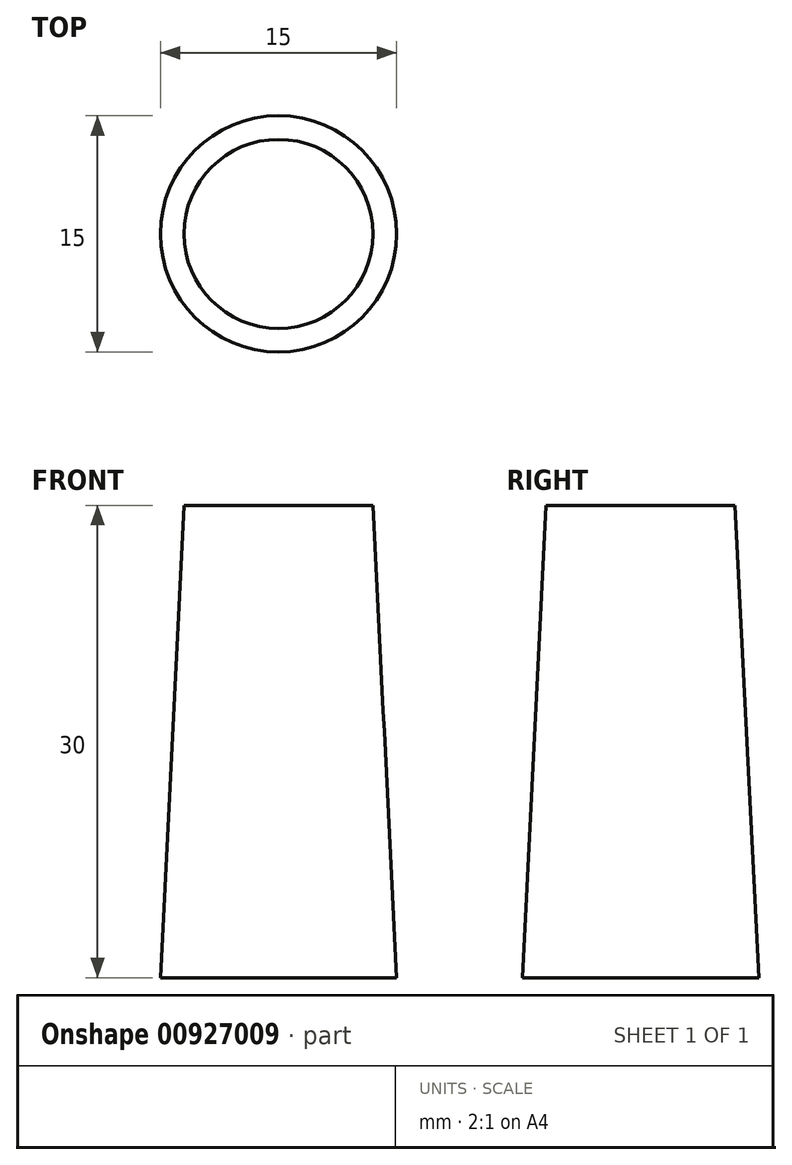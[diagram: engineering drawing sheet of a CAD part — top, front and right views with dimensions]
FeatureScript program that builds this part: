
annotation { "Feature Type Name" : "Feature", "Feature Type Description" : "" }
export const myFeature = defineFeature(function(context is Context, id is Id, definition is map)
    precondition{}
    {
        {
            assignVariable(context, id + "F0", {"name" : "height", "anyValue" : 30});
        }
        {
            var Q0;
            Q0=qCreatedBy(makeId("Top.planeOp"),FACE);
            cPlane(context, id + "F1", {"entities" : qUnion([Q0]), "cplaneType" : CPlaneType.OFFSET, "offset" : (getVariable(context, 'height')) * mm, "oppositeDirection" : true, "width" : 150 * mm, "height" : 150 * mm});
        }
        {
            var Q0;
            Q0=qCreatedBy(makeId("Top.planeOp"),FACE);
            var sketch = newSketch(context, id + "F2", { "sketchPlane" : qUnion([Q0])});
            skCircle(sketch, "E0", {"center": v(0, 0) * mm, "radius": 6 * mm});
            skSolve(sketch);
        }
        {
            var Q0;
            Q0=qCreatedBy(id+"F1.planeOp",FACE);
            var sketch = newSketch(context, id + "F3", { "sketchPlane" : qUnion([Q0])});
            skPoint(sketch, "E1.0", {"position": v(0, 0) * mm});
            skCircle(sketch, "E2", {"center": v(0, 0) * mm, "radius": 7.5 * mm});
            skSolve(sketch);
        }
        {
            var Q0;
            Q0=makeQuery(id+"F2.imprint","IMPRINT",FACE,{"disambiguationData":[TD([[makeQuery(id+"F2.imprint","IMPRINT",EDGE,{"derivedFrom":sQuery(id+"F2.wireOp",EDGE,"E0")}),1.0]])]});
            var Q1;
            Q1=makeQuery(id+"F3.imprint","IMPRINT",FACE,{"disambiguationData":[TD([[makeQuery(id+"F3.imprint","IMPRINT",EDGE,{"derivedFrom":sQuery(id+"F3.wireOp",EDGE,"E2")}),1.0]])]});
            loft(context, id + "F4", {"sheetProfilesArray" : [{ "sheetProfileEntities" : qUnion([Q0]) }, { "sheetProfileEntities" : qUnion([Q1]) }]});
        }
    });
